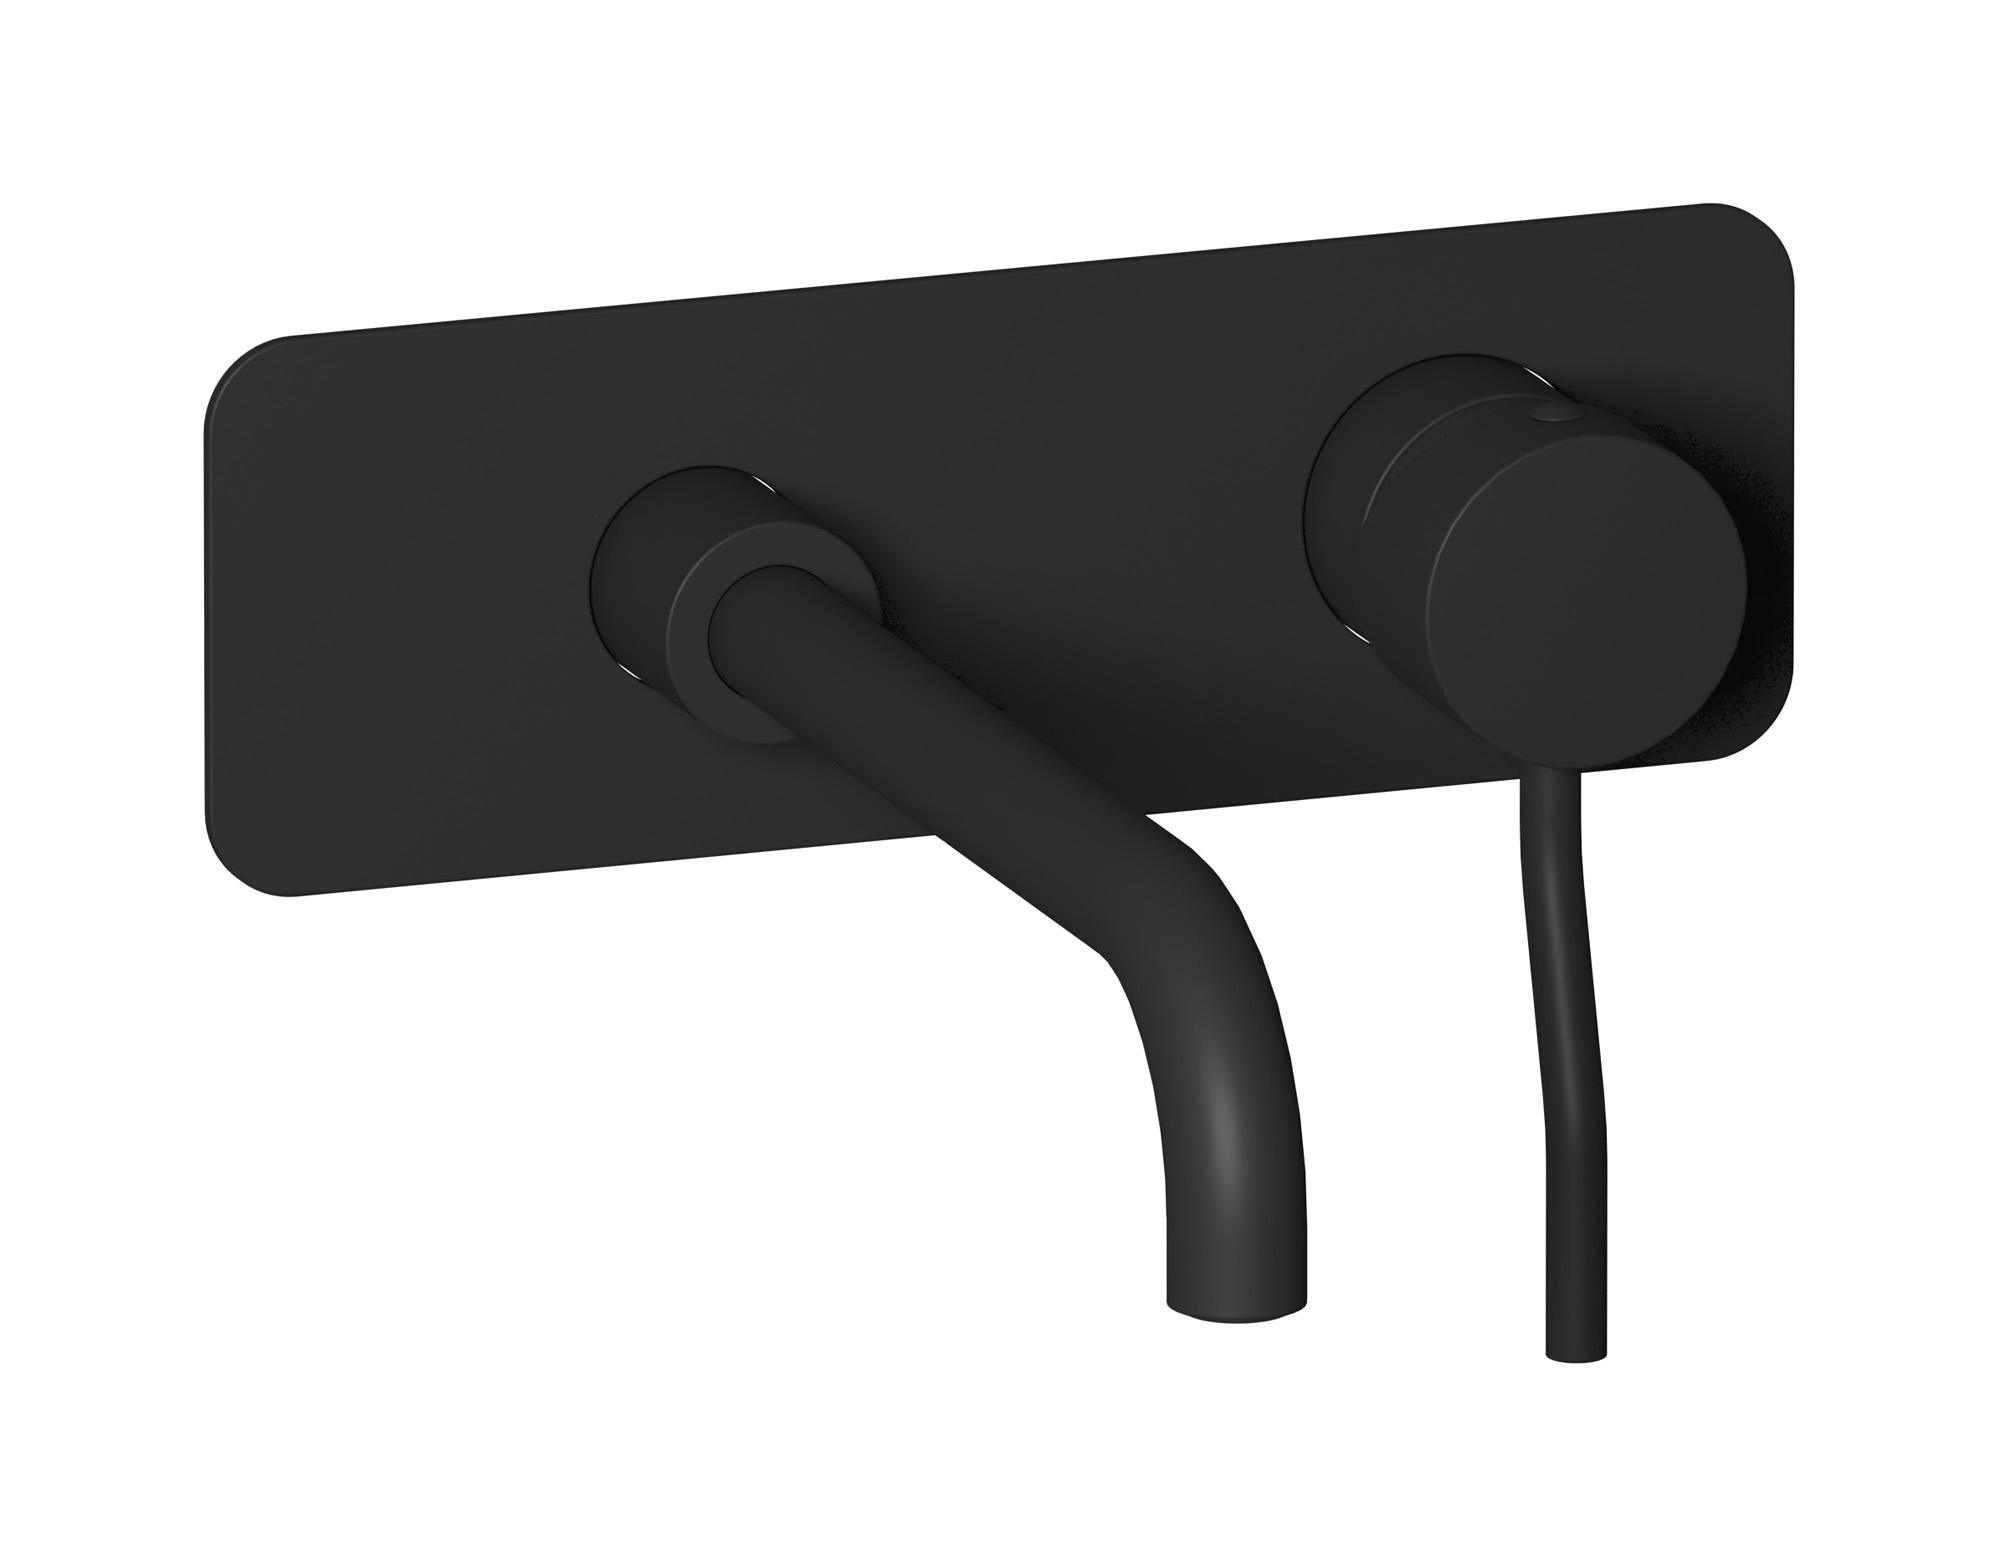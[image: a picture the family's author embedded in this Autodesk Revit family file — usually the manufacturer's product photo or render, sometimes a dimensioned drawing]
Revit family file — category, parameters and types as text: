
# Revit family: KU206
name_source: partatom
category: Apparecchi idraulici
units: mm (PartAtom-declared; Revit-internal decimal feet)

## family parameters
Basato su piano di lavoro = No
Condiviso = No
Mantieni orientamento annotazione = No
Numero OmniClass = 23.45.55.17
Punto di calcolo locali = No
Quota connettore circolare = Usa diametro
Sempre verticale = Sì
Taglio con vuoti quando caricato = No
Tipo di parte = Normale
Titolo OmniClass = Mixing Faucets

## types (3) — shared parameters
Cold water inlet = 10 mm  [stored 0.0328084 ft]
Commenti sul tipo = Wall mounted washbasin mixer complete with drain
Connessione CW = No
Connessione HW = No
Connessione di scarico = No
Connessione di ventilazione = No
Descrizione = Wall mounted washbasin mixer complete with drain
Hot water inlet = 10 mm  [stored 0.0328084 ft]
Produttore = IB Rubinetterie S.p.A.
URL = https://www.weareib.it
zero-valued in all types: Prospetto di default

## per-type parameters (varying)
| type | Finishes surface | Immagine tipo | Modello |
| Chrome | IB_Chrome | KU206CC.jpg | KU206CC |
| Matt Black | IB_matt black | KU206NP.jpg | KU206NP |
| Brushed Nickel | IB_Brushed nickel | KU206SS.jpg | KU206SS |

note: [stored X ft] marks values corroborated as IEEE doubles in the binary element streams (Revit-internal decimal feet)
